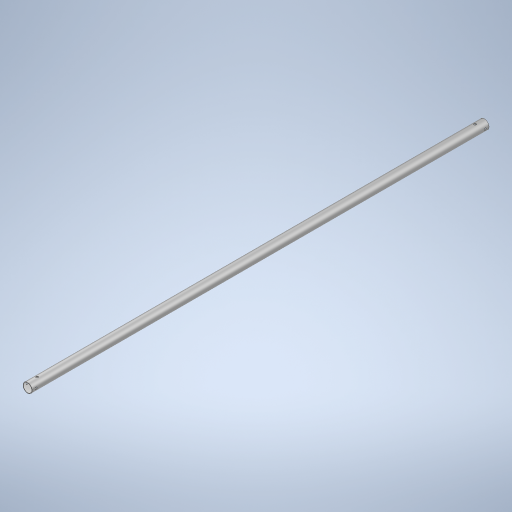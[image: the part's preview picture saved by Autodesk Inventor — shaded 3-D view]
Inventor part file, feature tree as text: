
AUTODESK INVENTOR PART (.ipt)
format: ipt  version: 2024 (Build 280153000, 153)  size: 282,112 bytes
history: native  units: in
note: dims shown in document units (in); Inventor stores cm internally (conversion verified against a paired STEP export)
features: sketch x4, extrude x3, plane x2, other x1
ambient origin geometry x8: Origin, YZ Plane, XZ Plane, XY Plane, X Axis, Y Axis, Z Axis, Center Point
bodies: Solid1 (feature_tree)
feature tree (10):
  sketch  "Sketch1"  dims[d0=2.374in d1=2.122in]
  extrude  "Extrusion1"  Depth=2.122in
  extrude  "Extrusion2"  TaperAngle=0.0deg  [1 undecoded]
  extrude  "Extrusion3"  Depth=0.9843in
  plane  "Work Plane1"
  plane  "Work Plane2"
  sketch  "Sketch2"  dims[d2=113.7795in d3=0.0in]
  sketch  "Sketch3"  dims[d5=3.937in d6=0.0in d7=0.9843in]
  sketch  "Sketch4"  dims[d8=0.5512in d9=2.3622in d10=3.937in d11=0.0in d12=1.187in d13=-1.187in]
  other  "Finish1"
note: 1 required parameter value undecoded (feature->parameter linkage not recoverable at this tier; creation-order binding heuristic only, values carry confidence <= 0.55)
